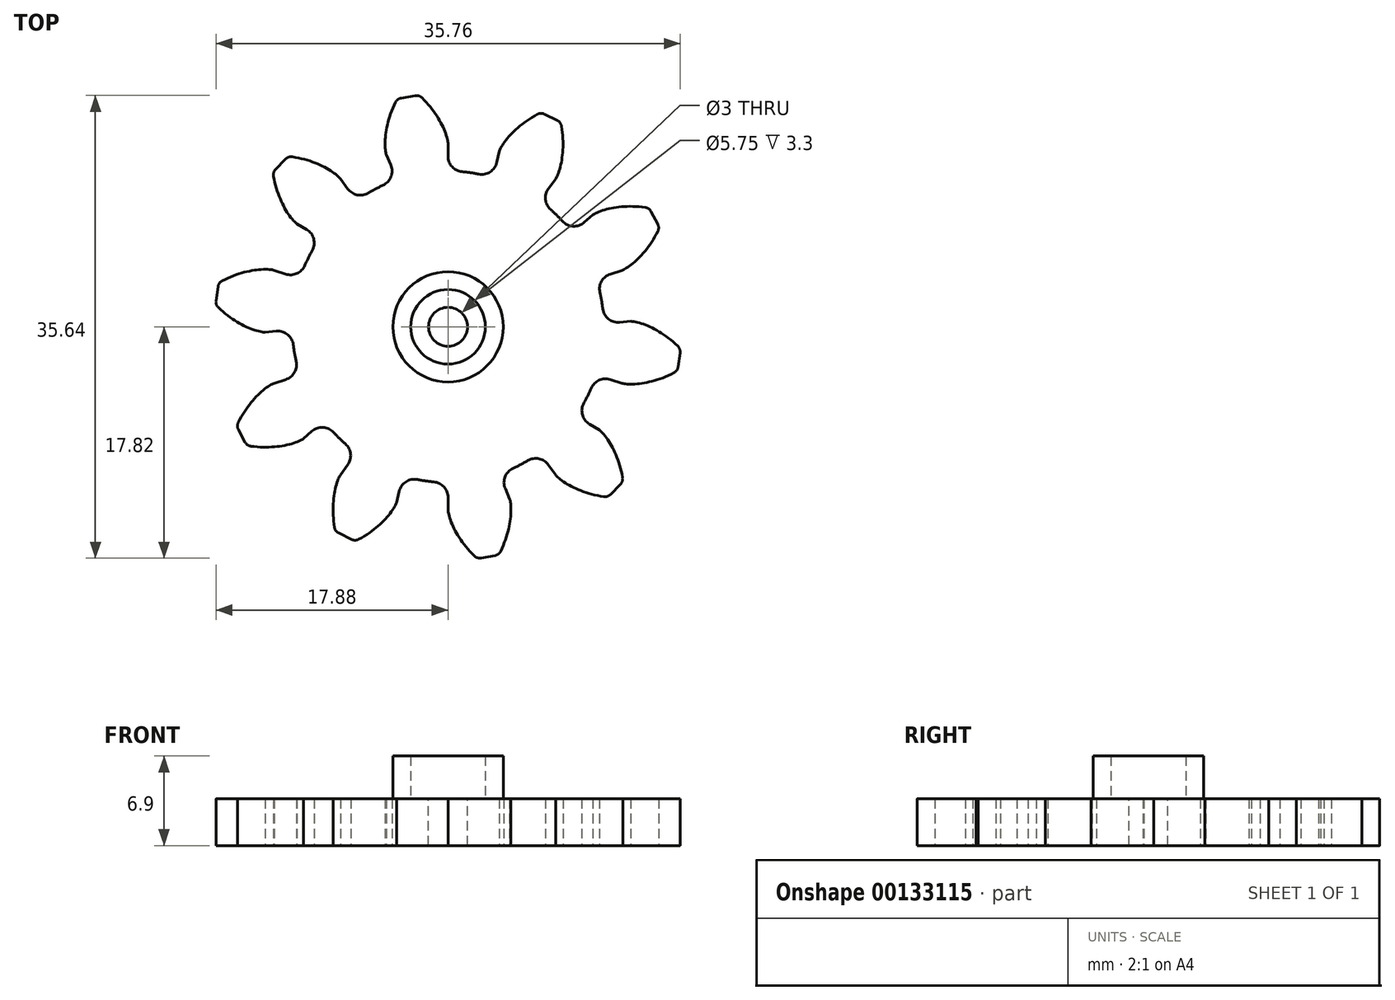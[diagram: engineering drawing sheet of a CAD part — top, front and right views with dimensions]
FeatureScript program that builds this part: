
annotation { "Feature Type Name" : "Feature", "Feature Type Description" : "" }
export const myFeature = defineFeature(function(context is Context, id is Id, definition is map)
    precondition{}
    {
        {
            var Q0;
            Q0=qCreatedBy(makeId("Top.planeOp"),FACE);
            var sketch = newSketch(context, id + "F0", { "sketchPlane" : qUnion([Q0])});
            skCircle(sketch, "E0", {"center": v(0, 0) * mm, "radius": 20 * mm});
            skCircle(sketch, "E1", {"center": v(0, 0) * mm, "radius": 25 * mm, "construction": true});
            skCircle(sketch, "E2", {"center": v(0, 0) * mm, "radius": 30 * mm, "construction": true});
            skLineSegment(sketch, "E3", {"start": v(0, 0) * mm, "end": v(14.22, 39.06) * mm, "construction": true});
            skLineSegment(sketch, "E4", {"start": v(0, 25) * mm, "end": v(-31, 25) * mm, "construction": true});
            skLineSegment(sketch, "E5", {"start": v(0, 25) * mm, "end": v(-27.58, 35.04) * mm, "construction": true});
            skLineSegment(sketch, "E6", {"start": v(0, 25) * mm, "end": v(62.1, 2.4) * mm, "construction": true});
            skCircle(sketch, "E7", {"center": v(0, 0) * mm, "radius": 23.5 * mm, "construction": true});
            skLineSegment(sketch, "E8", {"start": v(0, 0) * mm, "end": v(7.1, -40.26) * mm, "construction": true});
            skLineSegment(sketch, "E9", {"start": v(4.08, -23.14) * mm, "end": v(0.04, -23.85) * mm, "construction": true});
            skLineSegment(sketch, "E10", {"start": v(0, 0) * mm, "end": v(15.02, -41.26) * mm, "construction": true});
            skLineSegment(sketch, "E11", {"start": v(0, 0) * mm, "end": v(23.32, -40.38) * mm, "construction": true});
            skLineSegment(sketch, "E12", {"start": v(8.03, -22.08) * mm, "end": v(0.33, -24.88) * mm, "construction": true});
            skLineSegment(sketch, "E13", {"start": v(11.75, -20.34) * mm, "end": v(1.1, -26.5) * mm, "construction": true});
            skLineSegment(sketch, "E14", {"start": v(0, 0) * mm, "end": v(36.23, -43.18) * mm, "construction": true});
            skLineSegment(sketch, "E15", {"start": v(0, 0) * mm, "end": v(43.28, -36.31) * mm, "construction": true});
            skLineSegment(sketch, "E16", {"start": v(15.1, -18) * mm, "end": v(2.54, -28.54) * mm, "construction": true});
            skLineSegment(sketch, "E17", {"start": v(18, -15.1) * mm, "end": v(4.82, -30.8) * mm, "construction": true});
            skFitSpline(sketch, "E18", {"points": [v(0, -23.5) * mm, v(0.04, -23.85) * mm, v(0.33, -24.88) * mm, v(1.1, -26.5) * mm, v(2.54, -28.54) * mm, v(4.82, -30.8) * mm], "startDerivative": vector(0.25, -3.32) * mm, "endDerivative": vector(8.58, -7.94) * mm});
            skPoint(sketch, "E19", {"position": v(3.72, -29.77) * mm});
            skPoint(sketch, "E20", {"position": v(0.37, -25) * mm});
            skLineSegment(sketch, "E21", {"start": v(0, 0) * mm, "end": v(0.37, -25) * mm, "construction": true});
            skLineSegment(sketch, "E22", {"start": v(0, 0) * mm, "end": v(5.79, -33.31) * mm, "construction": true});
            skFitSpline(sketch, "E23.MirrorCS", {"points": [v(7.92, -22.12) * mm, v(8, -22.46) * mm, v(8.08, -23.53) * mm, v(7.9, -25.31) * mm, v(7.23, -27.72) * mm, v(5.85, -30.63) * mm], "startDerivative": vector(0.88, -3.2) * mm, "endDerivative": vector(-5.4, -10.37) * mm});
            skPoint(sketch, "E24.MirrorP", {"position": v(6.54, -29.28) * mm});
            skLineSegment(sketch, "E25", {"start": v(3.72, -29.77) * mm, "end": v(6.54, -29.28) * mm});
            skLineSegment(sketch, "E26", {"start": v(7.92, -22.12) * mm, "end": v(6.54, -18.9) * mm});
            skLineSegment(sketch, "E27", {"start": v(0, -23.5) * mm, "end": v(0, -20) * mm});
            skSolve(sketch);
        }
        {
            var Q0;
            Q0 = qSketchRegion(id + "F0", true);
            extrude(context, id + "F1", {"entities" : qUnion([Q0]), "depth" : 6 * mm});
        }
        {
            var Q0;
            Q0=makeQuery(id+"F1.opExtrude","SWEPT_EDGE",EDGE,{"disambiguationData":[OSD([sQuery(id+"F0.wireOp",EDGE,"E0"),sQuery(id+"F0.wireOp",EDGE,"E26")])]});
            var Q1;
            Q1=makeQuery(id+"F1.opExtrude","SWEPT_EDGE",EDGE,{"disambiguationData":[OSD([sQuery(id+"F0.wireOp",EDGE,"E0"),sQuery(id+"F0.wireOp",EDGE,"E27")])]});
            fillet(context, id + "F2", {"entities" : qUnion([Q0, Q1]), "radius" : 2 * mm, "tangentPropagation" : true, "allowEdgeOverflow" : false});
        }
        {
            var Q0;
            Q0=makeQuery(id+"F1.opExtrude","SWEPT_EDGE",EDGE,{"disambiguationData":[OSD([sQuery(id+"F0.wireOp",EDGE,"E23.MirrorCS"),sQuery(id+"F0.wireOp",EDGE,"E25")])]});
            var Q1;
            Q1=makeQuery(id+"F1.opExtrude","SWEPT_EDGE",EDGE,{"disambiguationData":[OSD([sQuery(id+"F0.wireOp",EDGE,"E18"),sQuery(id+"F0.wireOp",EDGE,"E25")])]});
            fillet(context, id + "F3", {"entities" : qUnion([Q0, Q1]), "radius" : 1 * mm, "tangentPropagation" : true, "allowEdgeOverflow" : false});
        }
        {
            var Q0;
            Q0=qCreatedBy(makeId("Front.planeOp"),FACE);
            var sketch = newSketch(context, id + "F4", { "sketchPlane" : qUnion([Q0])});
            skLineSegment(sketch, "E28", {"start": v(0, 0) * mm, "end": v(0, 37.8) * mm, "construction": true});
            skSolve(sketch);
        }
        {
            var Q0;
            Q0=makeQuery(id+"F1.opExtrude","SWEPT_BODY",BODY,{"disambiguationData":[OSD([sQuery(id+"F0.wireOp",EDGE,"E0"),sQuery(id+"F0.wireOp",EDGE,"E18"),sQuery(id+"F0.wireOp",EDGE,"E23.MirrorCS"),sQuery(id+"F0.wireOp",EDGE,"E25"),sQuery(id+"F0.wireOp",EDGE,"E26"),sQuery(id+"F0.wireOp",EDGE,"E27")])]});
            var Q1;
            Q1=sQuery(id+"F4.wireOp",EDGE,"E28");
            circularPattern(context, id + "F5", {"operationType" : NewBodyOperationType.ADD, "entities" : qUnion([Q0]), "axis" : qUnion([Q1]), "angle" : 36 * degree, "instanceCount" : 10});
        }
        {
            var Q0;
            Q0=makeQuery(id+"F1.opExtrude","SWEPT_BODY",BODY,{"disambiguationData":[OSD([sQuery(id+"F0.wireOp",EDGE,"E0"),sQuery(id+"F0.wireOp",EDGE,"E18"),sQuery(id+"F0.wireOp",EDGE,"E23.MirrorCS"),sQuery(id+"F0.wireOp",EDGE,"E25"),sQuery(id+"F0.wireOp",EDGE,"E26"),sQuery(id+"F0.wireOp",EDGE,"E27")])]});
            var Q1;
            Q1=qCreatedBy(makeId("Origin.pointOp"),VERTEX);
            transform(context, id + "F6", {"entities" : qUnion([Q0]), "transformType" : TransformType.SCALE_UNIFORMLY, "scale" : 0.6, "scalePoint" : qUnion([Q1]), "makeCopy" : false});
        }
        {
            var Q0;
            {var subQ0=makeQuery(id+"F1.opExtrude","CAP_FACE",FACE,{"disambiguationData":[OSD([sQuery(id+"F0.wireOp",EDGE,"E0"),sQuery(id+"F0.wireOp",EDGE,"E18"),sQuery(id+"F0.wireOp",EDGE,"E23.MirrorCS"),sQuery(id+"F0.wireOp",EDGE,"E25"),sQuery(id+"F0.wireOp",EDGE,"E26"),sQuery(id+"F0.wireOp",EDGE,"E27")])],"isStart":false});Q0=makeQuery(id+"F5.boolean.opBoolean","MERGE",FACE,{"derivedFrom":[subQ0,makeQuery(id+"F5.opPattern","COPY",FACE,{"derivedFrom":subQ0,"instanceName":"1"}),makeQuery(id+"F5.opPattern","COPY",FACE,{"derivedFrom":subQ0,"instanceName":"2"}),makeQuery(id+"F5.opPattern","COPY",FACE,{"derivedFrom":subQ0,"instanceName":"3"}),makeQuery(id+"F5.opPattern","COPY",FACE,{"derivedFrom":subQ0,"instanceName":"4"}),makeQuery(id+"F5.opPattern","COPY",FACE,{"derivedFrom":subQ0,"instanceName":"5"}),makeQuery(id+"F5.opPattern","COPY",FACE,{"derivedFrom":subQ0,"instanceName":"6"}),makeQuery(id+"F5.opPattern","COPY",FACE,{"derivedFrom":subQ0,"instanceName":"7"}),makeQuery(id+"F5.opPattern","COPY",FACE,{"derivedFrom":subQ0,"instanceName":"8"}),makeQuery(id+"F5.opPattern","COPY",FACE,{"derivedFrom":subQ0,"instanceName":"9"})]});}
            var sketch = newSketch(context, id + "F7", { "sketchPlane" : qUnion([Q0])});
            skCircle(sketch, "E29", {"center": v(0, 0) * mm, "radius": 2.88 * mm});
            skCircle(sketch, "E30", {"center": v(0, 0) * mm, "radius": 4.25 * mm});
            skCircle(sketch, "E31", {"center": v(0, 0) * mm, "radius": 1.5 * mm});
            skSolve(sketch);
        }
        {
            var Q0;
            Q0=makeQuery(id+"F7.imprint","IMPRINT",FACE,{"disambiguationData":[TD([[makeQuery(id+"F7.imprint","IMPRINT",EDGE,{"derivedFrom":sQuery(id+"F7.wireOp",EDGE,"E31")}),1.0]])]});
            extrude(context, id + "F8", {"entities" : qUnion([Q0]), "operationType" : NewBodyOperationType.REMOVE, "endBound" : BoundingType.THROUGH_ALL, "oppositeDirection" : true, "depth" : 25 * mm});
        }
        {
            var Q0;
            Q0=makeQuery(id+"F7.imprint","IMPRINT",FACE,{"disambiguationData":[TD([[makeQuery(id+"F7.imprint","IMPRINT",EDGE,{"derivedFrom":sQuery(id+"F7.wireOp",EDGE,"E29")}),-1.0]])]});
            extrude(context, id + "F9", {"entities" : qUnion([Q0]), "operationType" : NewBodyOperationType.ADD, "depth" : 3.3 * mm});
        }
    });
